# Revit family: Window-Double_Hung-Pella-Architect_Series-Fixed
name_source: partatom
category: Windows
revit_build: Autodesk Revit Architecture 2013 (Build: 20130531_2115(x64)
units: mm (PartAtom-declared; Revit-internal decimal feet)

## types (32) — shared parameters
Analytic Construction = <None>
Architectural Design Manual = To be determined
Construction Type = -
Cross Grille Pattern = No
Custom Grille Pattern = No
Custom Horizontal Lites = 2
Custom Vertical Lites = 3
Default Sill Height = 3' - 0"
Description = Double Hung - Fixed Unit
Egress Window = No
Energy Efficiency = http://www.pella.com
Environmental Commitment = http://www.pella.com
Ext Finish = Aluminum - Pella - Brown
Glazing Finish = Glass - Pella - Clear Insulating Glass
Glazing Thickness = 0' - 0 163/256"
Grille Visibility = Yes
Int Finish = Wood - Pella - Pine
Manufacturer = Pella Windows & Doors
Operation = Fixed
Prairie Grille Pattern = No
Product Documentation Link = http://media.pella.com
Product Name = Architect Series Double-Hung Window
Product Page URL = http://www.pella.com
Series = Architect Series - Aluminum-Clad Wood
Size Constraints = Window Sizing constraints available in 6.35 mm increments
Top Row Grille Pattern = No
Traditional Grille Pattern = Yes
URL = www.pella.com
Wall Closure = By host

## per-type parameters (varying)
| type | Head Height | Height | Rough Height | Rough Width | Sash Height | Sash Width | Unit Height | Unit Width | Width |
| 4135 | 5' - 11" | 2' - 11" | 2' - 11 3/4" | 3' - 5 3/4" | 2' - 8 1/2" | 3' - 2 1/2" | 2' - 11" | 3' - 5" | 3' - 5" |
| 4141 | 6' - 5" | 3' - 5" | 3' - 5 3/4" | 3' - 5 3/4" | 3' - 2 1/2" | 3' - 2 1/2" | 3' - 5" | 3' - 5" | 3' - 5" |
| 4147 | 6' - 11" | 3' - 11" | 3' - 11 3/4" | 3' - 5 3/4" | 3' - 8 1/2" | 3' - 2 1/2" | 3' - 11" | 3' - 5" | 3' - 5" |
| 4153 | 7' - 5" | 4' - 5" | 4' - 5 3/4" | 3' - 5 3/4" | 4' - 2 1/2" | 3' - 2 1/2" | 4' - 5" | 3' - 5" | 3' - 5" |
| 4157 | 7' - 9" | 4' - 9" | 4' - 9 3/4" | 3' - 5 3/4" | 4' - 6 1/2" | 3' - 2 1/2" | 4' - 9" | 3' - 5" | 3' - 5" |
| 4159 | 7' - 11" | 4' - 11" | 4' - 11 3/4" | 3' - 5 3/4" | 4' - 8 1/2" | 3' - 2 1/2" | 4' - 11" | 3' - 5" | 3' - 5" |
| 4165 | 8' - 5" | 5' - 5" | 5' - 5 3/4" | 3' - 5 3/4" | 5' - 2 1/2" | 3' - 2 1/2" | 5' - 5" | 3' - 5" | 3' - 5" |
| 4171 | 8' - 11" | 5' - 11" | 5' - 11 3/4" | 3' - 5 3/4" | 5' - 8 1/2" | 3' - 2 1/2" | 5' - 11" | 3' - 5" | 3' - 5" |
| 4735 | 5' - 11" | 2' - 11" | 2' - 11 3/4" | 3' - 11 3/4" | 2' - 8 1/2" | 3' - 8 1/2" | 2' - 11" | 3' - 11" | 3' - 11" |
| 4741 | 6' - 5" | 3' - 5" | 3' - 5 3/4" | 3' - 11 3/4" | 3' - 2 1/2" | 3' - 8 1/2" | 3' - 5" | 3' - 11" | 3' - 11" |
| 4747 | 6' - 11" | 3' - 11" | 3' - 11 3/4" | 3' - 11 3/4" | 3' - 8 1/2" | 3' - 8 1/2" | 3' - 11" | 3' - 11" | 3' - 11" |
| 4753 | 7' - 5" | 4' - 5" | 4' - 5 3/4" | 3' - 11 3/4" | 4' - 2 1/2" | 3' - 8 1/2" | 4' - 5" | 3' - 11" | 3' - 11" |
| 4757 | 7' - 9" | 4' - 9" | 4' - 9 3/4" | 3' - 11 3/4" | 4' - 6 1/2" | 3' - 8 1/2" | 4' - 9" | 3' - 11" | 3' - 11" |
| 4759 | 7' - 11" | 4' - 11" | 4' - 11 3/4" | 3' - 11 3/4" | 4' - 8 1/2" | 3' - 8 1/2" | 4' - 11" | 3' - 11" | 3' - 11" |
| 4765 | 8' - 5" | 5' - 5" | 5' - 5 3/4" | 3' - 11 3/4" | 5' - 2 1/2" | 3' - 8 1/2" | 5' - 5" | 3' - 11" | 3' - 11" |
| 4771 | 8' - 11" | 5' - 11" | 5' - 11 3/4" | 3' - 11 3/4" | 5' - 8 1/2" | 3' - 8 1/2" | 5' - 11" | 3' - 11" | 3' - 11" |
| 5335 | 5' - 11" | 2' - 11" | 2' - 11 3/4" | 4' - 5 3/4" | 2' - 8 1/2" | 4' - 2 1/2" | 2' - 11" | 4' - 5" | 4' - 5" |
| 5341 | 6' - 5" | 3' - 5" | 3' - 5 3/4" | 4' - 5 3/4" | 3' - 2 1/2" | 4' - 2 1/2" | 3' - 5" | 4' - 5" | 4' - 5" |
| 5347 | 6' - 11" | 3' - 11" | 3' - 11 3/4" | 4' - 5 3/4" | 3' - 8 1/2" | 4' - 2 1/2" | 3' - 11" | 4' - 5" | 4' - 5" |
| 5353 | 7' - 5" | 4' - 5" | 4' - 5 3/4" | 4' - 5 3/4" | 4' - 2 1/2" | 4' - 2 1/2" | 4' - 5" | 4' - 5" | 4' - 5" |
| 5357 | 7' - 9" | 4' - 9" | 4' - 9 3/4" | 4' - 5 3/4" | 4' - 6 1/2" | 4' - 2 1/2" | 4' - 9" | 4' - 5" | 4' - 5" |
| 5359 | 7' - 11" | 4' - 11" | 4' - 11 3/4" | 4' - 5 3/4" | 4' - 8 1/2" | 4' - 2 1/2" | 4' - 11" | 4' - 5" | 4' - 5" |
| 5365 | 8' - 5" | 5' - 5" | 5' - 5 3/4" | 4' - 5 3/4" | 5' - 2 1/2" | 4' - 2 1/2" | 5' - 5" | 4' - 5" | 4' - 5" |
| 5371 | 8' - 11" | 5' - 11" | 5' - 11 3/4" | 4' - 5 3/4" | 5' - 8 1/2" | 4' - 2 1/2" | 5' - 11" | 4' - 5" | 4' - 5" |
| 5935 | 5' - 11" | 2' - 11" | 2' - 11 3/4" | 4' - 11 3/4" | 2' - 8 1/2" | 4' - 8 1/2" | 2' - 11" | 4' - 11" | 4' - 11" |
| 5941 | 6' - 5" | 3' - 5" | 3' - 5 3/4" | 4' - 11 3/4" | 3' - 2 1/2" | 4' - 8 1/2" | 3' - 5" | 4' - 11" | 4' - 11" |
| 5947 | 6' - 11" | 3' - 11" | 3' - 11 3/4" | 4' - 11 3/4" | 3' - 8 1/2" | 4' - 8 1/2" | 3' - 11" | 4' - 11" | 4' - 11" |
| 5953 | 7' - 5" | 4' - 5" | 4' - 5 3/4" | 4' - 11 3/4" | 4' - 2 1/2" | 4' - 8 1/2" | 4' - 5" | 4' - 11" | 4' - 11" |
| 5957 | 7' - 9" | 4' - 9" | 4' - 9 3/4" | 4' - 11 3/4" | 4' - 6 1/2" | 4' - 8 1/2" | 4' - 9" | 4' - 11" | 4' - 11" |
| 5959 | 7' - 11" | 4' - 11" | 4' - 11 3/4" | 4' - 11 3/4" | 4' - 8 1/2" | 4' - 8 1/2" | 4' - 11" | 4' - 11" | 4' - 11" |
| 5965 | 8' - 5" | 5' - 5" | 5' - 5 3/4" | 4' - 11 3/4" | 5' - 2 1/2" | 4' - 8 1/2" | 5' - 5" | 4' - 11" | 4' - 11" |
| 5971 | 8' - 11" | 5' - 11" | 5' - 11 3/4" | 4' - 11 3/4" | 5' - 8 1/2" | 4' - 8 1/2" | 5' - 11" | 4' - 11" | 4' - 11" |

note: column(s) folded — value = type name in every type: Model

## geometry (parser evidence)
native form markers: Blend x14, Sweep x7
no freeform markers — native parametric forms only
